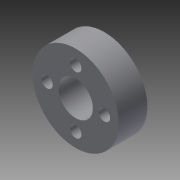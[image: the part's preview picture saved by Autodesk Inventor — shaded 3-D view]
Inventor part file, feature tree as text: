
AUTODESK INVENTOR PART (.ipt)
format: ipt  version: 2015 (Build 190159000, 159)  size: 94,720 bytes
history: native  units: mm
features: extrude x1, sketch x1
ambient origin geometry x8: Origin, YZ Plane, XZ Plane, XY Plane, X Axis, Y Axis, Z Axis, Center Point
bodies: Solid1 (feature_tree)
feature tree (2):
  extrude  "Extrusion1"  Depth=10.0mm
  sketch  "Sketch1"  dims[d0=30.0mm d2=4.0mm d3=4.0mm d4=4.0mm d5=4.0mm d6=12.0mm d7=10.0mm d8=0.0mm]
